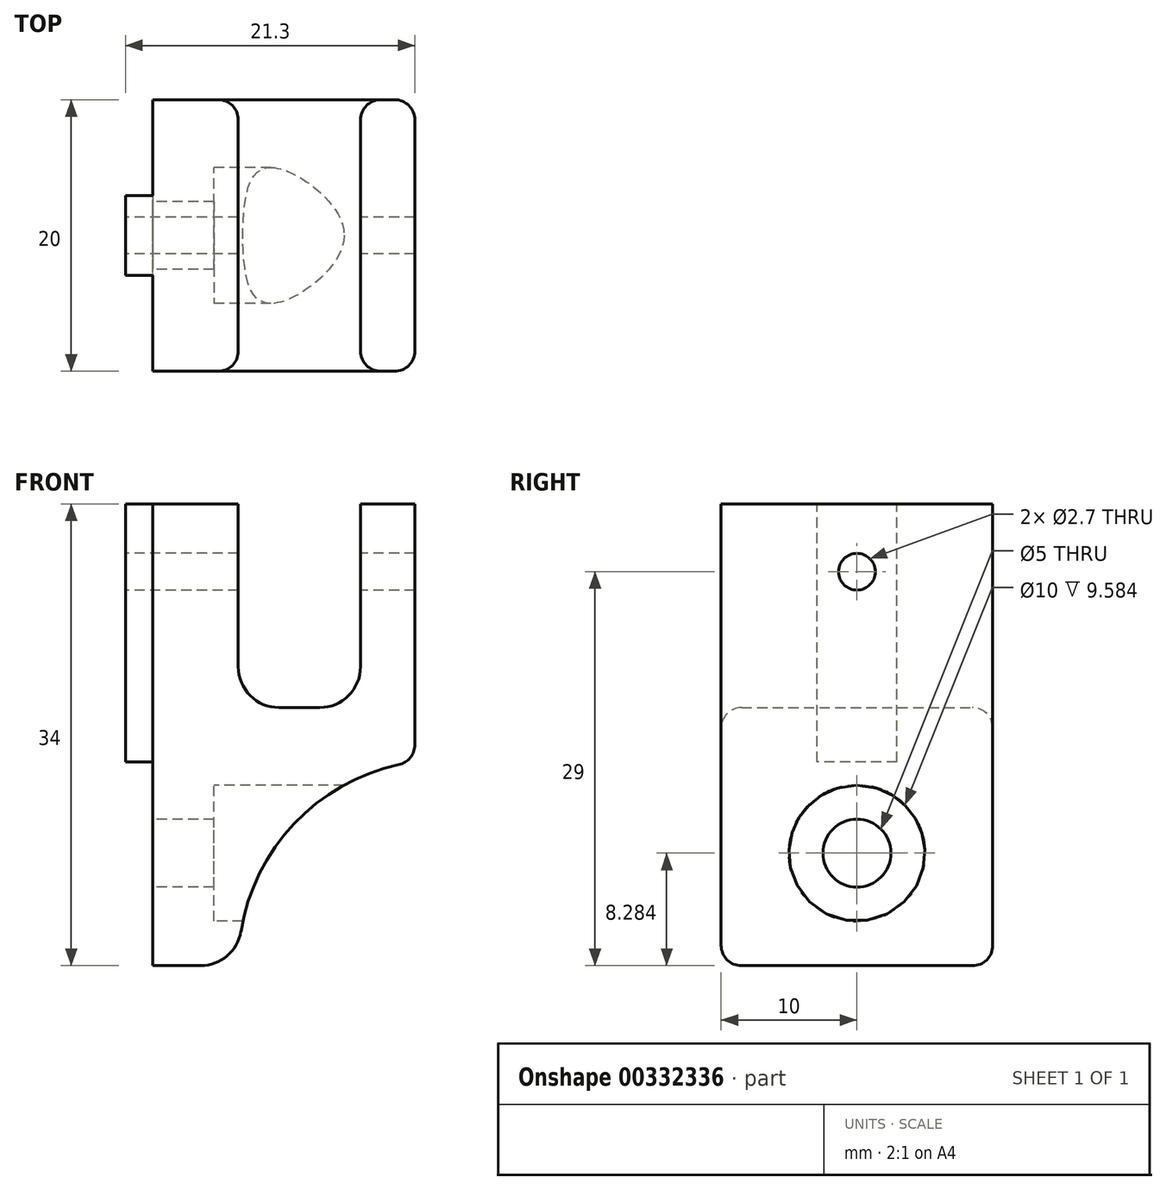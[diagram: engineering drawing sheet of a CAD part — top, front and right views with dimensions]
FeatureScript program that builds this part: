
annotation { "Feature Type Name" : "Feature", "Feature Type Description" : "" }
export const myFeature = defineFeature(function(context is Context, id is Id, definition is map)
    precondition{}
    {
        {
            var Q0;
            Q0=qCreatedBy(makeId("Front.planeOp"),FACE);
            var sketch = newSketch(context, id + "F0", { "sketchPlane" : qUnion([Q0])});
            skLineSegment(sketch, "E0.bottom", {"start": v(0, 0) * mm, "end": v(6.3, 0) * mm});
            skLineSegment(sketch, "E0.right", {"start": v(6.3, 0) * mm, "end": v(6.3, 15) * mm});
            skLineSegment(sketch, "E1.bottom", {"start": v(15.3, 34) * mm, "end": v(19.3, 34) * mm});
            skLineSegment(sketch, "E1.left", {"start": v(15.3, 34) * mm, "end": v(15.3, 19) * mm});
            skLineSegment(sketch, "E2.bottom", {"start": v(15.3, 19) * mm, "end": v(6.3, 19) * mm});
            skLineSegment(sketch, "E2.top", {"start": v(19.3, 15) * mm, "end": v(6.3, 15) * mm});
            skLineSegment(sketch, "E3", {"start": v(19.3, 34) * mm, "end": v(19.3, 15) * mm});
            skLineSegment(sketch, "E4", {"start": v(6.3, 19) * mm, "end": v(6.3, 34) * mm});
            skLineSegment(sketch, "E5", {"start": v(6.3, 34) * mm, "end": v(0, 34) * mm});
            skLineSegment(sketch, "E6", {"start": v(0, 34) * mm, "end": v(0, 0) * mm});
            skSolve(sketch);
        }
        {
            var Q0;
            {var subQ1=sQuery(id+"F0.wireOp",EDGE,"E0.bottom");Q0=makeQuery(id+"F0.imprint","IMPRINT",FACE,{"disambiguationData":[TD([[makeQuery(id+"F0.imprint","IMPRINT",EDGE,{"derivedFrom":subQ1}),1.0]])]});}
            var Q1;
            Q1=makeQuery(id+"F0.imprint","IMPRINT",FACE,{"disambiguationData":[TD([[makeQuery(id+"F0.imprint","IMPRINT",EDGE,{"derivedFrom":sQuery(id+"F0.wireOp",EDGE,"E2.top")}),-1.0]])]});
            var Q2;
            Q2=makeQuery(id+"F0.imprint","IMPRINT",FACE,{"disambiguationData":[TD([[makeQuery(id+"F0.imprint","IMPRINT",EDGE,{"derivedFrom":sQuery(id+"F0.wireOp",EDGE,"E1.bottom")}),-1.0]])]});
            extrude(context, id + "F1", {"entities" : qUnion([Q0, Q1, Q2]), "depth" : 10 * mm, "hasSecondDirection" : true, "secondDirectionOppositeDirection" : true, "secondDirectionDepth" : 10 * mm, "offsetDistance" : 25 * mm});
        }
        {
            var Q0;
            Q0=makeQuery(id+"F1.opExtrude","SWEPT_EDGE",EDGE,{"disambiguationData":[OSD([sQuery(id+"F0.wireOp",EDGE,"E0.right"),sQuery(id+"F0.wireOp",EDGE,"E2.top"),sQuery(id+"F0.wireOp",EDGE,"E2.right")])]});
            fillet(context, id + "F2", {"entities" : qUnion([Q0]), "radius" : 15 * mm, "tangentPropagation" : true, "allowEdgeOverflow" : false});
        }
        {
            var Q0;
            Q0=makeQuery(id+"F1.opExtrude","SWEPT_EDGE",EDGE,{"disambiguationData":[OSD([sQuery(id+"F0.wireOp",EDGE,"E0.right"),sQuery(id+"F0.wireOp",EDGE,"E2.bottom"),sQuery(id+"F0.wireOp",EDGE,"E2.right")])]});
            var Q1;
            Q1=makeQuery(id+"F1.opExtrude","SWEPT_EDGE",EDGE,{"disambiguationData":[OSD([sQuery(id+"F0.wireOp",EDGE,"E1.left"),sQuery(id+"F0.wireOp",EDGE,"E2.bottom")])]});
            fillet(context, id + "F3", {"entities" : qUnion([Q0, Q1]), "radius" : 3 * mm, "tangentPropagation" : true, "allowEdgeOverflow" : false});
        }
        {
            var Q0;
            Q0=qCreatedBy(makeId("Top.planeOp"),FACE);
            var sketch = newSketch(context, id + "F4", { "sketchPlane" : qUnion([Q0])});
            skLineSegment(sketch, "E7.bottom", {"start": v(-2, 2.95) * mm, "end": v(2, 2.95) * mm});
            skLineSegment(sketch, "E7.top", {"start": v(-2, -2.95) * mm, "end": v(2, -2.95) * mm});
            skLineSegment(sketch, "E7.left", {"start": v(-2, 2.95) * mm, "end": v(-2, -2.95) * mm});
            skLineSegment(sketch, "E7.right", {"start": v(2, 2.95) * mm, "end": v(2, -2.95) * mm});
            skPoint(sketch, "E7.middle", {"position": v(0, 0) * mm});
            skSolve(sketch);
        }
        {
            var Q0;
            Q0=makeQuery(id+"F4.imprint","IMPRINT",FACE,{"disambiguationData":[TD([[makeQuery(id+"F4.imprint","IMPRINT",EDGE,{"derivedFrom":sQuery(id+"F4.wireOp",EDGE,"E7.bottom")}),-1.0]])]});
            extrude(context, id + "F5", {"entities" : qUnion([Q0]), "operationType" : NewBodyOperationType.ADD, "depth" : 34 * mm, "offsetDistance" : 25 * mm, "hasSecondDirection" : true, "secondDirectionOppositeDirection" : false, "secondDirectionDepth" : 15 * mm});
        }
        {
            var Q0;
            Q0=qCreatedBy(makeId("Right.planeOp"),FACE);
            var sketch = newSketch(context, id + "F6", { "sketchPlane" : qUnion([Q0])});
            skCircle(sketch, "E8", {"center": v(0, 29) * mm, "radius": 1.35 * mm});
            skCircle(sketch, "E9", {"center": v(0, 8.28) * mm, "radius": 2.5 * mm});
            skCircle(sketch, "E10", {"center": v(0, 8.28) * mm, "radius": 5 * mm});
            skCircle(sketch, "E11", {"center": v(0, 8.28) * mm, "radius": 3.4 * mm});
            skSolve(sketch);
        }
        {
            var Q0;
            Q0=makeQuery(id+"F6.imprint","IMPRINT",FACE,{"disambiguationData":[TD([[makeQuery(id+"F6.imprint","IMPRINT",EDGE,{"derivedFrom":sQuery(id+"F6.wireOp",EDGE,"E8")}),1.0]])]});
            extrude(context, id + "F7", {"entities" : qUnion([Q0]), "operationType" : NewBodyOperationType.REMOVE, "depth" : 25 * mm, "hasSecondDirection" : true, "secondDirectionOppositeDirection" : true, "secondDirectionDepth" : 25 * mm});
        }
        {
            var Q0;
            Q0=makeQuery(id+"F6.imprint","IMPRINT",FACE,{"disambiguationData":[TD([[makeQuery(id+"F6.imprint","IMPRINT",EDGE,{"derivedFrom":sQuery(id+"F6.wireOp",EDGE,"E9")}),1.0]])]});
            extrude(context, id + "F8", {"entities" : qUnion([Q0]), "operationType" : NewBodyOperationType.REMOVE, "depth" : 15 * mm, "hasSecondDirection" : true, "secondDirectionOppositeDirection" : true, "secondDirectionDepth" : 10 * mm});
        }
        {
            var Q0;
            Q0=makeQuery(id+"F6.imprint","IMPRINT",FACE,{"disambiguationData":[TD([[makeQuery(id+"F6.imprint","IMPRINT",EDGE,{"derivedFrom":sQuery(id+"F6.wireOp",EDGE,"E9")}),-1.0]])]});
            var Q1;
            Q1=makeQuery(id+"F6.imprint","IMPRINT",FACE,{"disambiguationData":[TD([[makeQuery(id+"F6.imprint","IMPRINT",EDGE,{"derivedFrom":sQuery(id+"F6.wireOp",EDGE,"E10")}),1.0]])]});
            extrude(context, id + "F9", {"entities" : qUnion([Q0, Q1]), "operationType" : NewBodyOperationType.REMOVE, "depth" : 30 * mm, "hasSecondDirection" : true, "secondDirectionOppositeDirection" : false, "secondDirectionDepth" : 4.5 * mm, "offsetDistance" : 25 * mm});
        }
        {
            var Q0;
            Q0=makeQuery(id+"F6.imprint","IMPRINT",FACE,{"disambiguationData":[TD([[makeQuery(id+"F6.imprint","IMPRINT",EDGE,{"derivedFrom":sQuery(id+"F6.wireOp",EDGE,"E9")}),-1.0]])]});
            extrude(context, id + "F10", {"entities" : qUnion([Q0]), "operationType" : NewBodyOperationType.REMOVE, "oppositeDirection" : true, "depth" : 10 * mm, "hasDraft" : true, "draftAngle" : 40 * degree, "offsetDistance" : 25 * mm});
        }
        {
            var Q0;
            Q0=makeQuery(id+"FVQzFijdfIberP7_1.boolean.opBoolean","INTERSECT",EDGE,{"derivedFrom":[makeQuery(id+"F1.opExtrude","SWEPT_FACE",FACE,{"disambiguationData":[OSD([sQuery(id+"F0.wireOp",EDGE,"E1.bottom")])]}),makeQuery(id+"FVQzFijdfIberP7_1.opExtrude","SWEPT_FACE",FACE,{"disambiguationData":[OSD([sQuery(id+"FllVCIRI6JCQqES_1.wireOp",EDGE,"0gJeJJ1y-EJvm-fnZg-GKMm-UuW6JYeC1a1f")])]})]});
            var Q1;
            Q1=makeQuery(id+"F1.opExtrude","CAP_EDGE",EDGE,{"disambiguationData":[OSD([sQuery(id+"F0.wireOp",EDGE,"E0.top")])],"isStart":true});
            var Q2;
            Q2=makeQuery(id+"FVQzFijdfIberP7_1.boolean.opBoolean","INTERSECT",EDGE,{"derivedFrom":[makeQuery(id+"F1.opExtrude","SWEPT_FACE",FACE,{"disambiguationData":[OSD([sQuery(id+"F0.wireOp",EDGE,"E1.bottom")])]}),makeQuery(id+"FVQzFijdfIberP7_1.opExtrude","SWEPT_FACE",FACE,{"disambiguationData":[OSD([sQuery(id+"FllVCIRI6JCQqES_1.wireOp",EDGE,"ad4fdd70-2fb9-4313-b07b-df9d61838bc60.MirrorCS")])]})]});
            var Q3;
            Q3=makeQuery(id+"F1.opExtrude","CAP_EDGE",EDGE,{"disambiguationData":[OSD([sQuery(id+"F0.wireOp",EDGE,"E0.top")])],"isStart":false});
            var Q4;
            Q4=makeQuery(id+"F1.opExtrude","CAP_EDGE",EDGE,{"disambiguationData":[OSD([sQuery(id+"F0.wireOp",EDGE,"E0.bottom")])],"isStart":true});
            var Q5;
            Q5=makeQuery(id+"F1.opExtrude","CAP_EDGE",EDGE,{"disambiguationData":[OSD([sQuery(id+"F0.wireOp",EDGE,"E0.bottom")])],"isStart":false});
            var Q6;
            Q6=makeQuery(id+"F2.opFillet","BLEND_EDGE",EDGE,{"blendedFrom":[makeQuery(id+"F1.opExtrude","SWEPT_EDGE",EDGE,{"disambiguationData":[OSD([sQuery(id+"F0.wireOp",EDGE,"E0.right"),sQuery(id+"F0.wireOp",EDGE,"E2.top"),sQuery(id+"F0.wireOp",EDGE,"E2.right")])]}),makeQuery(id+"F1.opExtrude","SWEPT_FACE",FACE,{"disambiguationData":[OSD([sQuery(id+"F0.wireOp",EDGE,"E1.right"),sQuery(id+"F0.wireOp",EDGE,"E2.left")])]})],"blendedInto":[makeQuery(id+"F1.opExtrude","SWEPT_FACE",FACE,{"disambiguationData":[OSD([sQuery(id+"F0.wireOp",EDGE,"E1.right"),sQuery(id+"F0.wireOp",EDGE,"E2.left")])]})]});
            var Q7;
            Q7=makeQuery(id+"FVQzFijdfIberP7_1.boolean.opBoolean","INTERSECT",EDGE,{"derivedFrom":[makeQuery(id+"F2.opFillet","BLEND_FACE",FACE,{"disambiguationData":[OSD([sQuery(id+"F0.wireOp",EDGE,"E0.right"),sQuery(id+"F0.wireOp",EDGE,"E2.top"),sQuery(id+"F0.wireOp",EDGE,"E2.right")])]}),makeQuery(id+"FVQzFijdfIberP7_1.opExtrude","SWEPT_FACE",FACE,{"disambiguationData":[OSD([sQuery(id+"FllVCIRI6JCQqES_1.wireOp",EDGE,"ad4fdd70-2fb9-4313-b07b-df9d61838bc60.MirrorCS")])]})]});
            var Q8;
            Q8=makeQuery(id+"FVQzFijdfIberP7_1.boolean.opBoolean","COPY",EDGE,{"derivedFrom":makeQuery(id+"FVQzFijdfIberP7_1.opExtrude","SWEPT_EDGE",EDGE,{"disambiguationData":[OSD([sQuery(id+"FllVCIRI6JCQqES_1.wireOp",EDGE,"ad4fdd70-2fb9-4313-b07b-df9d61838bc60.MirrorCS"),sQuery(id+"FllVCIRI6JCQqES_1.wireOp",EDGE,"6d596fc3-1ca0-40c5-aee4-fe9f60dd68ae0.MirrorCS")])]})});
            var Q9;
            Q9=makeQuery(id+"FVQzFijdfIberP7_1.boolean.opBoolean","COPY",EDGE,{"derivedFrom":makeQuery(id+"FVQzFijdfIberP7_1.opExtrude","SWEPT_EDGE",EDGE,{"disambiguationData":[OSD([sQuery(id+"FllVCIRI6JCQqES_1.wireOp",EDGE,"0gJeJJ1y-EJvm-fnZg-GKMm-UuW6JYeC1a1f"),sQuery(id+"FllVCIRI6JCQqES_1.wireOp",EDGE,"ayhZilKi-yUaR-i3xm-yCP8-kIRGACUT5FV1")])]})});
            var Q10;
            Q10=makeQuery(id+"FVQzFijdfIberP7_1.boolean.opBoolean","INTERSECT",EDGE,{"derivedFrom":[makeQuery(id+"F2.opFillet","BLEND_FACE",FACE,{"disambiguationData":[OSD([sQuery(id+"F0.wireOp",EDGE,"E0.right"),sQuery(id+"F0.wireOp",EDGE,"E2.top"),sQuery(id+"F0.wireOp",EDGE,"E2.right")])]}),makeQuery(id+"FVQzFijdfIberP7_1.opExtrude","SWEPT_FACE",FACE,{"disambiguationData":[OSD([sQuery(id+"FllVCIRI6JCQqES_1.wireOp",EDGE,"0gJeJJ1y-EJvm-fnZg-GKMm-UuW6JYeC1a1f")])]})]});
            var Q11;
            {var subQ0=sQuery(id+"F0.wireOp",EDGE,"E0.right");Q11=makeQuery(id+"F1.opExtrude","CAP_EDGE",EDGE,{"disambiguationData":[OSD([subQ0]),TDD([makeQuery(id+"F0.imprint","IMPRINT",EDGE,{"disambiguationData":[TD([[makeQuery(id+"F0.imprint","INTERSECT",VERTEX,{"derivedFrom":[sQuery(id+"F0.wireOp",EDGE,"E0.top"),subQ0]}),1.0]])],"derivedFrom":subQ0})])],"isStart":false});}
            var Q12;
            Q12=makeQuery(id+"F3.opFillet","BLEND_EDGE",EDGE,{"blendedFrom":[makeQuery(id+"F1.opExtrude","SWEPT_EDGE",EDGE,{"disambiguationData":[OSD([sQuery(id+"F0.wireOp",EDGE,"E1.left"),sQuery(id+"F0.wireOp",EDGE,"E2.bottom")])]}),makeQuery(id+"FVQzFijdfIberP7_1.boolean.opBoolean","COPY",FACE,{"derivedFrom":makeQuery(id+"FVQzFijdfIberP7_1.opExtrude","SWEPT_FACE",FACE,{"disambiguationData":[OSD([sQuery(id+"FllVCIRI6JCQqES_1.wireOp",EDGE,"ad4fdd70-2fb9-4313-b07b-df9d61838bc60.MirrorCS")])]})})],"blendedInto":[makeQuery(id+"FVQzFijdfIberP7_1.boolean.opBoolean","COPY",FACE,{"derivedFrom":makeQuery(id+"FVQzFijdfIberP7_1.opExtrude","SWEPT_FACE",FACE,{"disambiguationData":[OSD([sQuery(id+"FllVCIRI6JCQqES_1.wireOp",EDGE,"ad4fdd70-2fb9-4313-b07b-df9d61838bc60.MirrorCS")])]})})]});
            var Q13;
            Q13=makeQuery(id+"FVQzFijdfIberP7_1.boolean.opBoolean","INTERSECT",EDGE,{"derivedFrom":[makeQuery(id+"F1.opExtrude","SWEPT_FACE",FACE,{"disambiguationData":[OSD([sQuery(id+"F0.wireOp",EDGE,"E2.bottom")])]}),makeQuery(id+"FVQzFijdfIberP7_1.opExtrude","SWEPT_FACE",FACE,{"disambiguationData":[OSD([sQuery(id+"FllVCIRI6JCQqES_1.wireOp",EDGE,"0gJeJJ1y-EJvm-fnZg-GKMm-UuW6JYeC1a1f")])]})]});
            var Q14;
            {var subQ0=sQuery(id+"F0.wireOp",EDGE,"E0.right");Q14=makeQuery(id+"F1.opExtrude","CAP_EDGE",EDGE,{"disambiguationData":[OSD([subQ0]),TDD([makeQuery(id+"F0.imprint","IMPRINT",EDGE,{"disambiguationData":[TD([[makeQuery(id+"F0.imprint","INTERSECT",VERTEX,{"derivedFrom":[sQuery(id+"F0.wireOp",EDGE,"E0.top"),subQ0]}),1.0]])],"derivedFrom":subQ0})])],"isStart":true});}
            var Q15;
            {var subQ0=sQuery(id+"F0.wireOp",EDGE,"E0.right");var subQ1=sQuery(id+"F0.wireOp",EDGE,"E2.right");var subQ2=sQuery(id+"F0.wireOp",EDGE,"E2.top");Q15=makeQuery(id+"F2.opFillet","BLEND_EDGE",EDGE,{"blendedFrom":[makeQuery(id+"F1.opExtrude","SWEPT_EDGE",EDGE,{"disambiguationData":[OSD([subQ0,subQ2,subQ1])]}),makeQuery(id+"F1.opExtrude","SWEPT_FACE",FACE,{"disambiguationData":[OSD([subQ0]),TDD([makeQuery(id+"F0.imprint","IMPRINT",EDGE,{"disambiguationData":[TD([[makeQuery(id+"F0.imprint","INTERSECT",VERTEX,{"derivedFrom":[sQuery(id+"F0.wireOp",EDGE,"E0.bottom"),subQ0]}),-1.0]])],"derivedFrom":subQ0})])]})],"blendedInto":[makeQuery(id+"F1.opExtrude","SWEPT_FACE",FACE,{"disambiguationData":[OSD([subQ0]),TDD([makeQuery(id+"F0.imprint","IMPRINT",EDGE,{"disambiguationData":[TD([[makeQuery(id+"F0.imprint","INTERSECT",VERTEX,{"derivedFrom":[sQuery(id+"F0.wireOp",EDGE,"E0.bottom"),subQ0]}),-1.0]])],"derivedFrom":subQ0})])]})]});}
            var Q16;
            Q16=makeQuery(id+"F2.opFillet","BLEND_EDGE",EDGE,{"blendedFrom":[makeQuery(id+"F1.opExtrude","SWEPT_EDGE",EDGE,{"disambiguationData":[OSD([sQuery(id+"F0.wireOp",EDGE,"E0.right"),sQuery(id+"F0.wireOp",EDGE,"E2.top")])]}),makeQuery(id+"F1.opExtrude","SWEPT_FACE",FACE,{"disambiguationData":[OSD([sQuery(id+"F0.wireOp",EDGE,"E3")])]})],"blendedInto":[makeQuery(id+"F1.opExtrude","SWEPT_FACE",FACE,{"disambiguationData":[OSD([sQuery(id+"F0.wireOp",EDGE,"E3")])]})]});
            var Q17;
            Q17=makeQuery(id+"F1.opExtrude","CAP_EDGE",EDGE,{"disambiguationData":[OSD([sQuery(id+"F0.wireOp",EDGE,"E3")])],"isStart":false});
            var Q18;
            Q18=makeQuery(id+"F1.opExtrude","CAP_EDGE",EDGE,{"disambiguationData":[OSD([sQuery(id+"F0.wireOp",EDGE,"E3")])],"isStart":true});
            var Q19;
            Q19=makeQuery(id+"F1.opExtrude","CAP_EDGE",EDGE,{"disambiguationData":[OSD([sQuery(id+"F0.wireOp",EDGE,"E1.left")])],"isStart":true});
            var Q20;
            Q20=makeQuery(id+"F1.opExtrude","CAP_EDGE",EDGE,{"disambiguationData":[OSD([sQuery(id+"F0.wireOp",EDGE,"E4")])],"isStart":false});
            fillet(context, id + "F11", {"entities" : qUnion([Q0, Q1, Q2, Q3, Q4, Q5, Q6, Q7, Q8, Q9, Q10, Q11, Q12, Q13, Q14, Q15, Q16, Q17, Q18, Q19, Q20]), "radius" : 1.5 * mm, "tangentPropagation" : true, "allowEdgeOverflow" : false});
        }
    });
